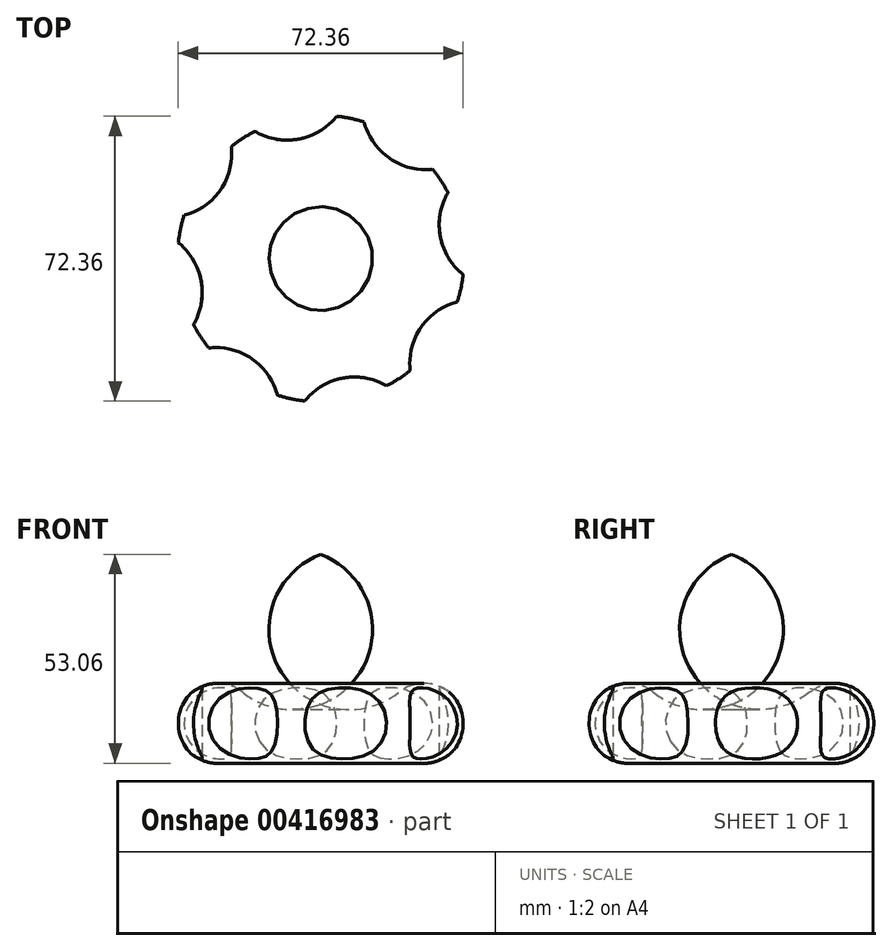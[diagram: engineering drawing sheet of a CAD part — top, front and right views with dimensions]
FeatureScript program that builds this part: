
annotation { "Feature Type Name" : "Feature", "Feature Type Description" : "" }
export const myFeature = defineFeature(function(context is Context, id is Id, definition is map)
    precondition{}
    {
        {
            var Q0;
            Q0=qCreatedBy(makeId("Front.planeOp"),FACE);
            var sketch = newSketch(context, id + "F0", { "sketchPlane" : qUnion([Q0])});
            skArc(sketch, "E0", {"start": v(-19.9, 18.1) * mm, "mid": v(-35.84, 13.52) * mm, "end": v(-26.25, 0) * mm});
            skArc(sketch, "E1", {"start": v(-19.9, 18.1) * mm, "mid": v(-10.37, 13.9) * mm, "end": v(0, 14.96) * mm});
            skLineSegment(sketch, "E2", {"start": v(0, 0) * mm, "end": v(0, 15) * mm});
            skLineSegment(sketch, "E3", {"start": v(0, 15) * mm, "end": v(0, 0) * mm});
            skLineSegment(sketch, "E4", {"start": v(0, 0) * mm, "end": v(-26.25, 0) * mm});
            skSolve(sketch);
        }
        {
            var Q0;
            Q0 = qSketchRegion(id + "F0", true);
            var Q1;
            Q1=sQuery(id+"F0.wireOp",EDGE,"E3");
            revolve(context, id + "F1", {"entities" : qUnion([Q0]), "axis" : qUnion([Q1]), "revolveType" : RevolveType.FULL});
        }
        {
            var Q0;
            Q0=qCreatedBy(makeId("Top.planeOp"),FACE);
            var sketch = newSketch(context, id + "F2", { "sketchPlane" : qUnion([Q0])});
            skCircle(sketch, "E5", {"center": v(-8.57, 46.26) * mm, "radius": 16.17 * mm});
            skCircle(sketch, "E6.1.0", {"center": v(-38.78, 26.65) * mm, "radius": 16.17 * mm});
            skCircle(sketch, "E6.2.0", {"center": v(-46.26, -8.57) * mm, "radius": 16.17 * mm});
            skCircle(sketch, "E6.3.0", {"center": v(-26.65, -38.78) * mm, "radius": 16.17 * mm});
            skCircle(sketch, "E6.4.0", {"center": v(8.57, -46.26) * mm, "radius": 16.17 * mm});
            skCircle(sketch, "E6.5.0", {"center": v(38.78, -26.65) * mm, "radius": 16.17 * mm});
            skCircle(sketch, "E6.6.0", {"center": v(46.26, 8.57) * mm, "radius": 16.17 * mm});
            skCircle(sketch, "E6.7.0", {"center": v(26.65, 38.78) * mm, "radius": 16.17 * mm});
            skPoint(sketch, "E6.center", {"position": v(0, 0) * mm});
            skSolve(sketch);
        }
        {
            var Q0;
            Q0 = qSketchRegion(id + "F2", true);
            extrude(context, id + "F3", {"entities" : qUnion([Q0]), "operationType" : NewBodyOperationType.REMOVE, "depth" : 41.66 * mm});
        }
    });
